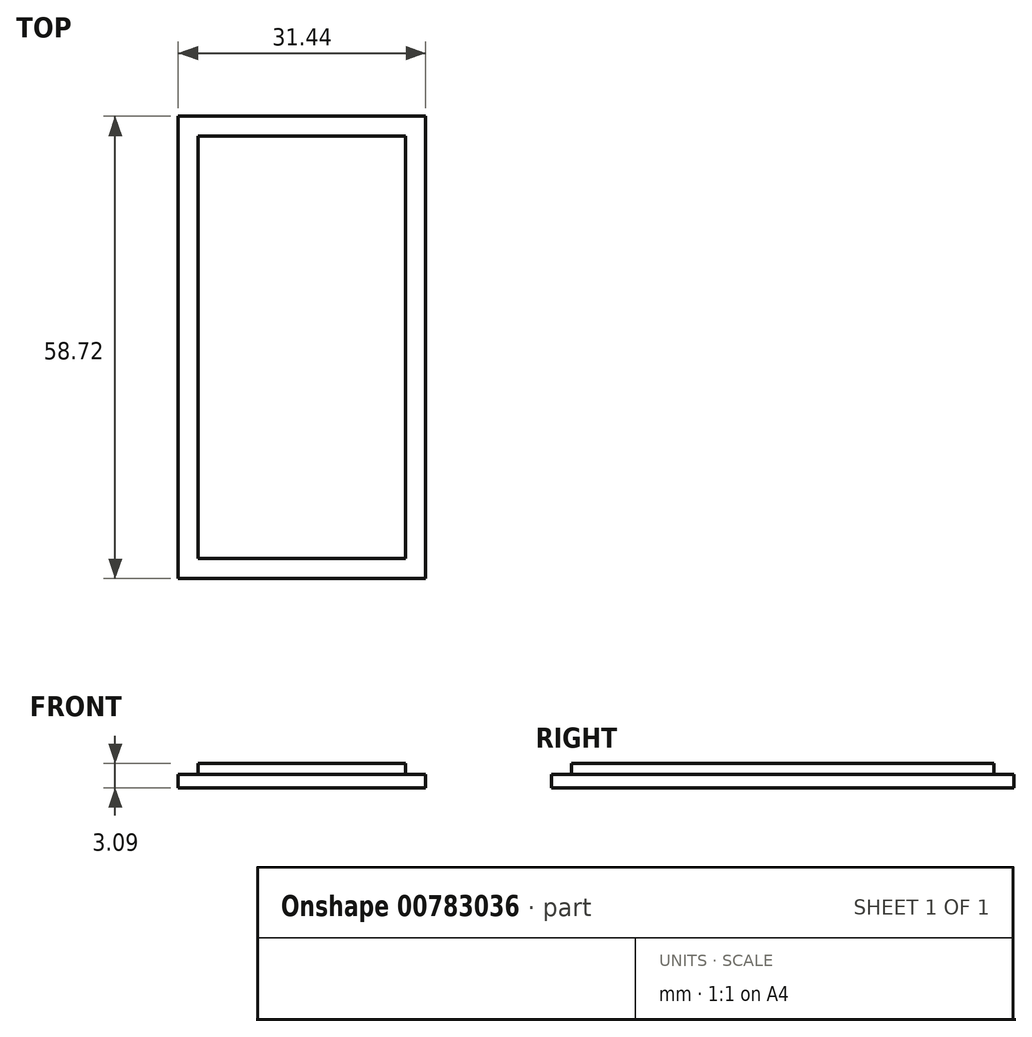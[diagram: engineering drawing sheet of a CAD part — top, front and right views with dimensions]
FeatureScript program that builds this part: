
annotation { "Feature Type Name" : "Feature", "Feature Type Description" : "" }
export const myFeature = defineFeature(function(context is Context, id is Id, definition is map)
    precondition{}
    {
        {
            var Q0;
            Q0=qCreatedBy(makeId("Top.planeOp"),FACE);
            var sketch = newSketch(context, id + "F0", { "sketchPlane" : qUnion([Q0])});
            skLineSegment(sketch, "E0.bottom", {"start": v(13.18, -26.82) * mm, "end": v(-13.18, -26.82) * mm});
            skLineSegment(sketch, "E0.top", {"start": v(13.18, 26.82) * mm, "end": v(-13.18, 26.82) * mm});
            skLineSegment(sketch, "E0.left", {"start": v(13.18, -26.82) * mm, "end": v(13.18, 26.82) * mm});
            skLineSegment(sketch, "E0.right", {"start": v(-13.18, -26.82) * mm, "end": v(-13.18, 26.82) * mm});
            skPoint(sketch, "E0.middle", {"position": v(0, 0) * mm});
            skSolve(sketch);
        }
        {
            var Q0;
            Q0=qCreatedBy(makeId("Top.planeOp"),FACE);
            var sketch = newSketch(context, id + "F1", { "sketchPlane" : qUnion([Q0])});
            skLineSegment(sketch, "E1.0", {"start": v(15.72, -29.36) * mm, "end": v(-15.72, -29.36) * mm});
            skLineSegment(sketch, "E1.1", {"start": v(15.72, -29.36) * mm, "end": v(15.72, 29.36) * mm});
            skLineSegment(sketch, "E1.2", {"start": v(15.72, 29.36) * mm, "end": v(-15.72, 29.36) * mm});
            skLineSegment(sketch, "E1.3", {"start": v(-15.72, -29.36) * mm, "end": v(-15.72, 29.36) * mm});
            skSolve(sketch);
        }
        {
            var Q0;
            Q0=makeQuery(id+"F0.imprint","IMPRINT",FACE,{"disambiguationData":[TD([[makeQuery(id+"F0.imprint","IMPRINT",EDGE,{"derivedFrom":sQuery(id+"F0.wireOp",EDGE,"E0.bottom")}),-1.0]])]});
            extrude(context, id + "F2", {"entities" : qUnion([Q0]), "depth" : 3.09 * mm, "offsetDistance" : 25.4 * mm});
        }
        {
            var Q0;
            Q0=makeQuery(id+"F1.imprint","IMPRINT",FACE,{"disambiguationData":[TD([[makeQuery(id+"F1.imprint","IMPRINT",EDGE,{"derivedFrom":sQuery(id+"F1.wireOp",EDGE,"E1.0")}),-1.0]])]});
            extrude(context, id + "F3", {"entities" : qUnion([Q0]), "operationType" : NewBodyOperationType.ADD, "depth" : 1.72 * mm, "offsetDistance" : 25.4 * mm});
        }
    });
